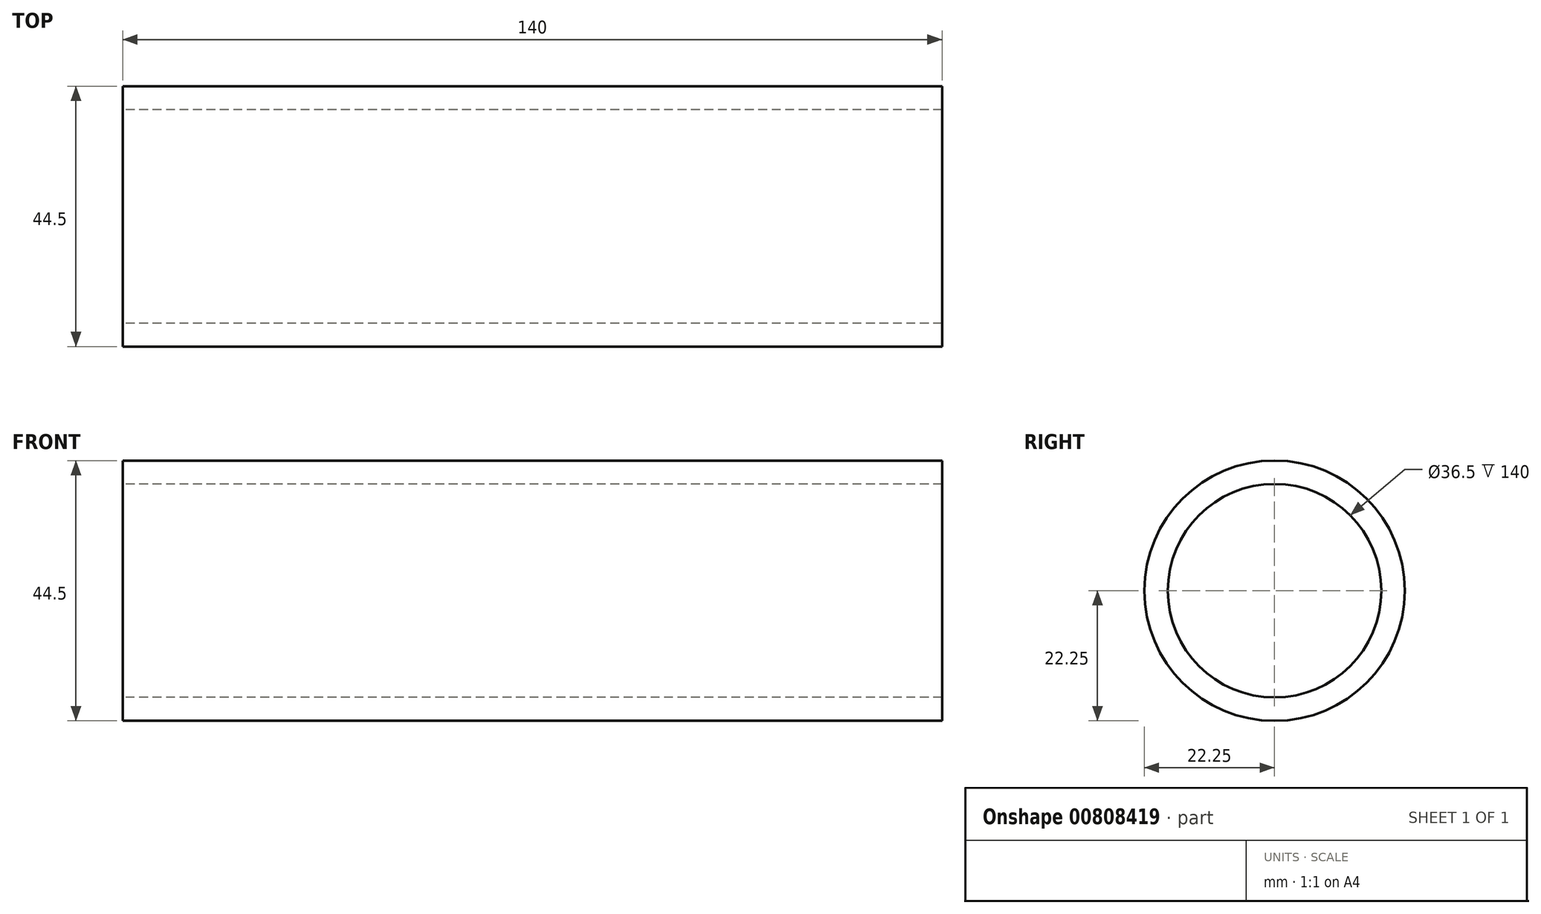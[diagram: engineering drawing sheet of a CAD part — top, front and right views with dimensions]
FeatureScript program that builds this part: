
annotation { "Feature Type Name" : "Feature", "Feature Type Description" : "" }
export const myFeature = defineFeature(function(context is Context, id is Id, definition is map)
    precondition{}
    {
        {
            var Q0;
            Q0=qCreatedBy(makeId("Right.planeOp"),FACE);
            var sketch = newSketch(context, id + "F0", { "sketchPlane" : qUnion([Q0])});
            skCircle(sketch, "E0", {"center": v(0, 0) * mm, "radius": 22.25 * mm});
            skCircle(sketch, "E1.0", {"center": v(0, 0) * mm, "radius": 18.25 * mm});
            skSolve(sketch);
        }
        {
            var Q0;
            Q0 = qSketchRegion(id + "F0", true);
            extrude(context, id + "F1", {"entities" : qUnion([Q0]), "depth" : 140 * mm, "offsetDistance" : 25 * mm});
        }
    });
